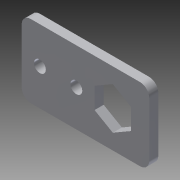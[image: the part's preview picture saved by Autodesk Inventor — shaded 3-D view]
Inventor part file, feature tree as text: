
AUTODESK INVENTOR PART (.ipt)
format: ipt  version: 2014 (Build 180170000, 170)  size: 100,352 bytes
history: native  units: in
note: dims shown in document units (in); Inventor stores cm internally (conversion verified against a paired STEP export)
features: extrude x1, fillet x1, sketch x1
ambient origin geometry x8: Origin, YZ Plane, XZ Plane, XY Plane, X Axis, Y Axis, Z Axis, Center Point
bodies: Solid1 (feature_tree)
feature tree (3):
  extrude  "Extrusion1"  Depth=1.0in
  fillet  "Fillet1"  Radius=0.163in
  sketch  "Sketch1"  dims[d0=1.75in d1=1.0in d2=0.163in d3=0.5in d4=0.25in d5=1.0in d6=0.5in d7=0.5in d8=0.125in d9=0.0in d10=0.125in d11=0.5in d12=0.5in]
